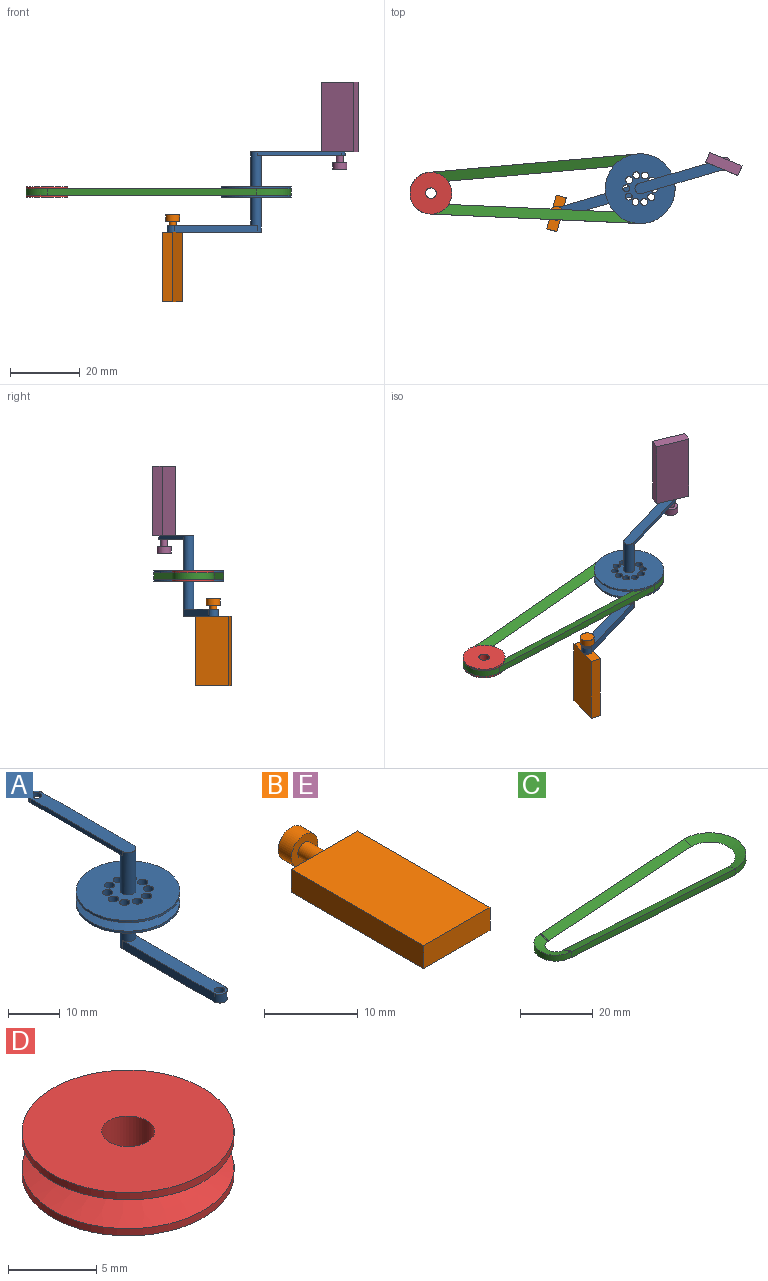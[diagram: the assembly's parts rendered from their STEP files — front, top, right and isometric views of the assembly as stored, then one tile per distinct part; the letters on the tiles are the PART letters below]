
ASSEMBLY  parts=5 mates=4
PART A: 30 faces, bbox 20x53x23 mm
  f0: cylinder r=1.5mm len=10mm, axis (0,0,-1), area 89.5mm2, adj f6,f7,f20,f21,f23
  f1: plane 20x20mm, normal (0,0,-1), area 275.7mm2, adj f2,f8,f10,f11,f12,f13,f14,f15
  f2: cylinder r=10mm len=20mm, axis (0,0,-1), area 31.4mm2, adj f1,f3
  f3: cone r=7mm half-angle=71.6deg, axis (0,0,-1), area 168.9mm2, adj f2,f4
  f4: cone r=10mm half-angle=71.6deg, axis (0,0,1), area 168.9mm2, adj f3,f5
  f5: cylinder r=10mm len=20mm, axis (0,0,-1), area 31.4mm2, adj f4,f6
  f6: plane 20x20mm, normal (0,0,1), area 275.7mm2, adj f0,f5,f10,f11,f12,f13,f14,f15
  f7: plane 28x3mm, normal (0,0,1), area 78.9mm2, adj f0,f21,f22,f23,f24
  f8: cylinder r=1.5mm len=10mm, axis (0,0,1), area 84.8mm2, adj f1,f9,f25,f26,f29
  f9: plane 28x3mm, normal (0,0,-1), area 78.9mm2, adj f8,f25,f26,f27,f28
  f10: cylinder r=1mm len=3mm, axis (0,0,1), area 18.8mm2, adj f1,f6
  f11: cylinder r=1mm len=3mm, axis (0,0,1), area 18.8mm2, adj f1,f6
  f12: cylinder r=1mm len=3mm, axis (0,0,1), area 18.8mm2, adj f1,f6
  f13: cylinder r=1mm len=3mm, axis (0,0,1), area 18.8mm2, adj f1,f6
  f14: cylinder r=1mm len=3mm, axis (0,0,1), area 18.8mm2, adj f1,f6
  f15: cylinder r=1mm len=3mm, axis (0,0,1), area 18.8mm2, adj f1,f6
  f16: cylinder r=1mm len=3mm, axis (0,0,1), area 18.8mm2, adj f1,f6
  f17: cylinder r=1mm len=3mm, axis (0,0,1), area 18.8mm2, adj f1,f6
  f18: cylinder r=1mm len=3mm, axis (0,0,1), area 18.8mm2, adj f1,f6
  f19: cylinder r=1mm len=3mm, axis (0,0,1), area 18.8mm2, adj f1,f6
  f20: plane 26.5x3mm, normal (0,0,-1), area 71.9mm2, adj f0,f21,f22,f23,f24
  f21: plane 25x1mm, normal (1,0,0), area 25mm2, adj f0,f7,f20,f22
  f22: cylinder r=1.5mm len=3mm, axis (0,0,1), area 4.7mm2, adj f7,f20,f21,f23
  f23: plane 25x1mm, normal (-1,0,0), area 25mm2, adj f0,f7,f20,f22
  f24: cylinder r=1mm len=2mm, axis (0,0,1), area 6.3mm2, adj f7,f20
  f25: plane 25x2mm, normal (-1,0,0), area 50mm2, adj f8,f9,f28,f29
  f26: plane 25x2mm, normal (1,0,0), area 50mm2, adj f8,f9,f28,f29
  f27: cylinder r=1mm len=2mm, axis (0,0,-1), area 12.6mm2, adj f9,f29
  f28: cylinder r=1.5mm len=3mm, axis (0,0,-1), area 9.4mm2, adj f9,f25,f26,f29
  f29: plane 26.5x3mm, normal (0,0,1), area 71.9mm2, adj f8,f25,f26,f27,f28
PART B: 10 faces, bbox 10x25x4 mm
  f0: cylinder r=1mm len=3mm, axis (0,-1,0), area 18.8mm2, adj f6,f8
  f1: plane 20x10mm, normal (0,0,-1), area 200mm2, adj f2,f4,f5,f6
  f2: plane 20x3mm, normal (1,0,0), area 60mm2, adj f1,f3,f5,f6
  f3: plane 20x10mm, normal (0,0,1), area 200mm2, adj f2,f4,f5,f6
  f4: plane 20x3mm, normal (-1,0,0), area 60mm2, adj f1,f3,f5,f6
  f5: plane 10x3mm, normal (0,-1,0), area 30mm2, adj f1,f2,f3,f4
  f6: plane 10x3mm, normal (0,1,0), area 26.9mm2, adj f0,f1,f2,f3,f4
  f7: cylinder r=2mm len=4mm, axis (0,1,0), area 25.1mm2, adj f8,f9
  f8: plane 4x4mm, normal (0,-1,0), area 9.4mm2, adj f0,f7
  f9: plane 4x4mm, normal (0,1,0), area 12.6mm2, adj f7
PART C: 38 faces, bbox 76x20.1x2 mm
  f0: plane 0.17x0.01mm, normal (-0.07,1,0), area 0mm2, adj f5,f11,f20
  f1: plane 60.03x4.01mm, normal (-0.07,1,0), area 120mm2, adj f9,f11,f15,f21
  f2: plane 60.03x4mm, normal (-0.07,-1,0), area 120mm2, adj f12,f13,f16,f17,f21
  f3: plane 3x1mm, normal (0.02,-0.32,-0.95), area 0.3mm2, adj f4,f5,f11,f36
  f4: plane 3.01x1.01mm, normal (0.02,-0.32,0.95), area 0.3mm2, adj f3,f10,f19,f37
  f5: plane 3.04x1.05mm, normal (-1,-0.07,0), area 0mm2, adj f0,f3,f11,f20
  f6: cone r=7mm half-angle=71.6deg, axis (0,0,-1), area 83.7mm2, adj f7,f8,f9,f14,f18
  f7: plane 0.05x0.02mm, normal (1,0,0), area 0mm2, adj f6,f13,f18
  f8: cone r=10mm half-angle=71.6deg, axis (0,0,1), area 83.8mm2, adj f6,f9,f15,f16,f17
  f9: cylinder r=10mm len=20mm, axis (0,0,-1), area 62.7mm2, adj f1,f6,f8,f12
  f10: plane 0.17x0.01mm, normal (-0.07,1,0), area 0mm2, adj f4,f19,f22
  f11: plane 60.2x4.02mm, normal (0,0,-1), area 0mm2, adj f0,f1,f3,f5,f14
  f12: plane 1.99x0mm, normal (1,0,0), area 0mm2, adj f2,f9,f13
  f13: plane 0.05x0mm, normal (0,0,-1), area 0mm2, adj f2,f7,f12,f18
  f14: plane 60x6.99mm, normal (0.02,-0.32,-0.95), area 189.2mm2, adj f6,f11,f15,f33,f34
  f15: plane 60.08x7.04mm, normal (0.02,-0.32,0.95), area 189.3mm2, adj f1,f8,f14,f33,f35
  f16: plane 60.05x7.02mm, normal (0.02,0.32,0.95), area 189.3mm2, adj f2,f8,f17,f29,f31
  f17: plane 60.24x7.01mm, normal (0.02,0.32,-0.95), area 189.6mm2, adj f2,f8,f16,f18,f26,f28
  f18: plane 3.03x1.04mm, normal (-1,0.07,0), area 0mm2, adj f6,f7,f13,f17
  f19: plane 3.04x1.05mm, normal (-1,-0.07,0), area 0mm2, adj f4,f10,f22
  f20: cone r=3mm half-angle=71.6deg, axis (0,0,-1), area 44.2mm2, adj f0,f5,f21,f22,f23,f25
  f21: cylinder r=6mm len=12mm, axis (0,0,-1), area 37.6mm2, adj f1,f2,f20,f22,f32
  f22: cone r=6mm half-angle=71.6deg, axis (0,0,1), area 44mm2, adj f10,f19,f20,f21,f32
  f23: plane 3.04x1.05mm, normal (-1,0.07,0), area 0mm2, adj f20,f24,f25
  f24: plane 3.01x1.01mm, normal (0.02,0.32,-0.95), area 0.3mm2, adj f23,f25,f27
  f25: plane 0.17x0.01mm, normal (-0.07,-1,0), area 0mm2, adj f20,f23,f24
  f26: plane 2.99x1mm, normal (1,0.04,0), area 0mm2, adj f17,f27,f28
  f27: cone r=3mm half-angle=71.6deg, axis (0,0,-1), area 0.7mm2, adj f24,f26,f28,f30
  f28: cylinder r=6mm len=0.29mm, axis (0,0,-1), area 0mm2, adj f17,f26,f27
  f29: plane 2.99x1mm, normal (1,0.04,0), area 0mm2, adj f16,f30,f31
  f30: cone r=6mm half-angle=71.6deg, axis (0,0,1), area 0.7mm2, adj f27,f29,f31,f32
  f31: cylinder r=6mm len=0.29mm, axis (0,0,-1), area 0mm2, adj f16,f29,f30
  f32: plane 3.05x1.05mm, normal (0.02,0.32,0.95), area 0.3mm2, adj f21,f22,f30
  f33: plane 3x2mm, normal (1,-0.04,0), area 0mm2, adj f14,f15,f34,f35,f36,f37
  f34: cylinder r=6mm len=0.26mm, axis (0,0,-1), area 0mm2, adj f14,f33,f36
  f35: cylinder r=6mm len=0.29mm, axis (0,0,-1), area 0mm2, adj f15,f33,f37
  f36: cone r=3mm half-angle=71.6deg, axis (0,0,-1), area 0.6mm2, adj f3,f33,f34,f37
  f37: cone r=6mm half-angle=71.6deg, axis (0,0,1), area 0.7mm2, adj f4,f33,f35,f36
PART D: 7 faces, bbox 12x12x3 mm
  f0: plane 12x12mm, normal (0,0,1), area 106mm2, adj f1,f6
  f1: cylinder r=1.5mm len=3mm, axis (0,0,1), area 28.3mm2, adj f0,f2
  f2: plane 12x12mm, normal (0,0,-1), area 106mm2, adj f1,f3
  f3: cylinder r=6mm len=12mm, axis (0,0,1), area 18.8mm2, adj f2,f4
  f4: cone r=3mm half-angle=71.6deg, axis (0,0,-1), area 89.4mm2, adj f3,f5
  f5: cone r=6mm half-angle=71.6deg, axis (0,0,1), area 89.4mm2, adj f4,f6
  f6: cylinder r=6mm len=12mm, axis (0,0,1), area 18.8mm2, adj f0,f5
PART E: same geometry as B
PLACE A rot(axis=(0,0,-1),73.6deg) t=(6.35,12.95,17.42)mm
PLACE B rot(axis=(0.68,0.52,0.52),111.5deg) t=(-17.63,5.89,7.42)mm
PLACE C rot(axis=(0,0,1),1.2deg) t=(6.35,12.95,17.92)mm
PLACE D t=(-53.63,11.66,17.42)mm fixed
PLACE E rot(axis=(-0.96,0.19,-0.19),92.2deg) t=(30.34,20,30.42)mm
MATE revolute D.f1 <-> C.f20  axis (0,0,1) through (-53.63,11.66,18.92)mm
MATE revolute E.f0 <-> A.f22  axis (0,0,1) through (30.34,20,30.42)mm
MATE revolute B.f0 <-> A.f27  axis (0,0,-1) through (-17.63,5.89,7.42)mm
MATE revolute A.f2 <-> C.f6  axis (0,0,-1) through (6.35,12.95,18.92)mm
